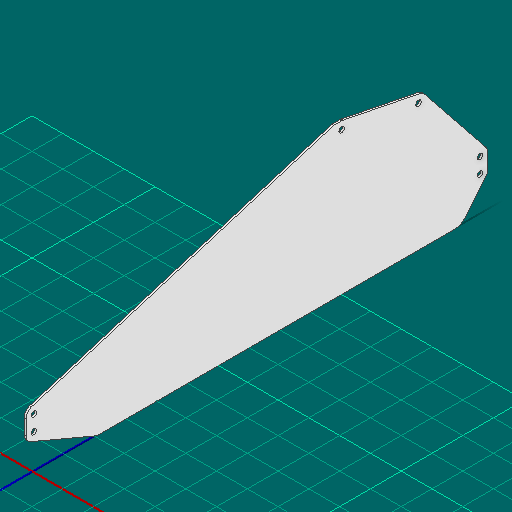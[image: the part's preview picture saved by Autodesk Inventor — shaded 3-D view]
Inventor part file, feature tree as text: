
AUTODESK INVENTOR PART (.ipt)
format: ipt  version: 2025 (Build 290162000, 162)  size: 122,368 bytes
history: native  units: in
note: dims shown in document units (in); Inventor stores cm internally (conversion verified against a paired STEP export)
features: other x3, extrude x1, sketch x1
ambient origin geometry x8: Origin, YZ Plane, XZ Plane, XY Plane, X Axis, Y Axis, Z Axis, Center Point
bodies: Solid1 (feature_tree)
feature tree (5):
  other  "Blocks"
  extrude  "Extrusion1"  Depth=0.0625in TaperAngle=0.0deg
  sketch  "Sketch1"  dims[d0=0.5in d1=0.5in d2=1.0in d3=0.0625in d4=0.0in]
  other  "maiin"
  other  "maiin:1"
